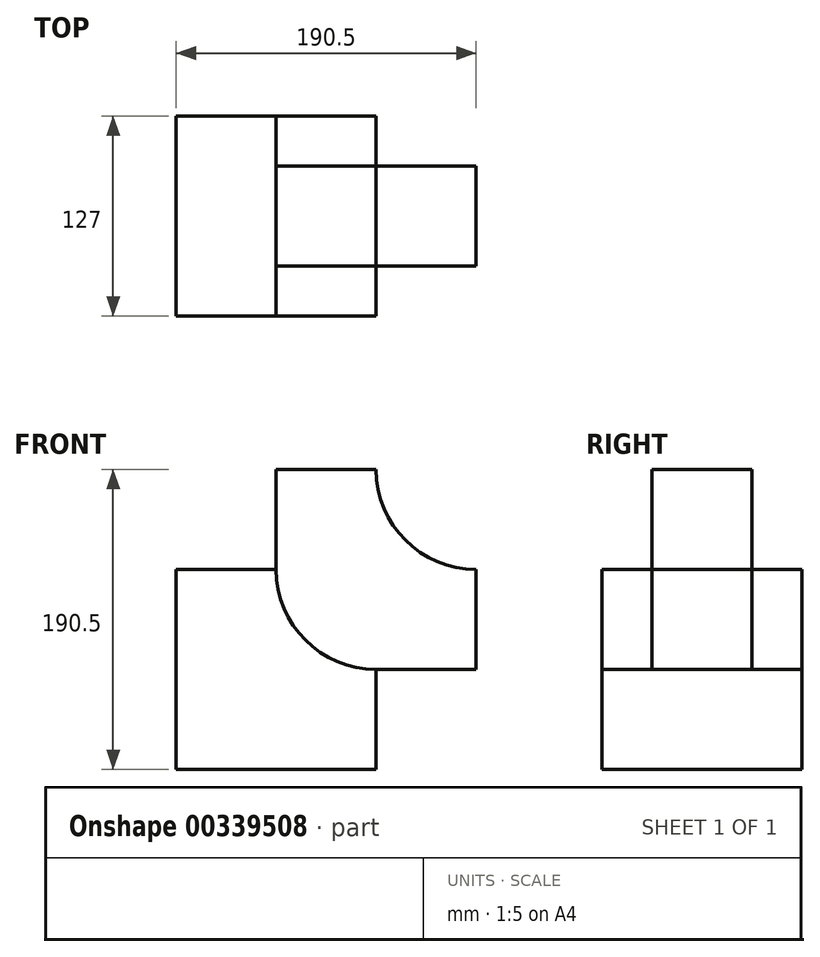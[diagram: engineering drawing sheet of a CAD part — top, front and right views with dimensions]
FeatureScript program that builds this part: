
annotation { "Feature Type Name" : "Feature", "Feature Type Description" : "" }
export const myFeature = defineFeature(function(context is Context, id is Id, definition is map)
    precondition{}
    {
        {
            var Q0;
            Q0=qCreatedBy(makeId("Front.planeOp"),FACE);
            var sketch = newSketch(context, id + "F0", { "sketchPlane" : qUnion([Q0])});
            skLineSegment(sketch, "E0.bottom", {"start": v(0, 63.5) * mm, "end": v(-63.5, 63.5) * mm});
            skLineSegment(sketch, "E0.top", {"start": v(63.5, -63.5) * mm, "end": v(-63.5, -63.5) * mm});
            skLineSegment(sketch, "E0.left", {"start": v(63.5, 0) * mm, "end": v(63.5, -63.5) * mm});
            skLineSegment(sketch, "E0.right", {"start": v(-63.5, 63.5) * mm, "end": v(-63.5, -63.5) * mm});
            skPoint(sketch, "E0.middle", {"position": v(0, 0) * mm});
            skArc(sketch, "E1", {"start": v(0, 63.5) * mm, "mid": v(18.6, 18.6) * mm, "end": v(63.5, 0) * mm});
            skSolve(sketch);
        }
        {
            var Q0;
            Q0=makeQuery(id+"F0.imprint","IMPRINT",FACE,{"disambiguationData":[TD([[makeQuery(id+"F0.imprint","IMPRINT",EDGE,{"derivedFrom":sQuery(id+"F0.wireOp",EDGE,"E0.bottom")}),1.0]])]});
            extrude(context, id + "F1", {"entities" : qUnion([Q0]), "endBound" : BoundingType.SYMMETRIC, "depth" : 127 * mm});
        }
        {
            var Q0;
            Q0=qCreatedBy(makeId("Front.planeOp"),FACE);
            var sketch = newSketch(context, id + "F2", { "sketchPlane" : qUnion([Q0])});
            skLineSegment(sketch, "E2.bottom", {"start": v(0, 0) * mm, "end": v(127, 0) * mm});
            skLineSegment(sketch, "E2.top", {"start": v(0, 127) * mm, "end": v(127, 127) * mm});
            skLineSegment(sketch, "E2.left", {"start": v(0, 0) * mm, "end": v(0, 127) * mm});
            skLineSegment(sketch, "E2.right", {"start": v(127, 0) * mm, "end": v(127, 127) * mm});
            skCircle(sketch, "E3", {"center": v(127, 127) * mm, "radius": 63.5 * mm});
            skSolve(sketch);
        }
        {
            var Q0;
            Q0=makeQuery(id+"F2.imprint","IMPRINT",FACE,{"disambiguationData":[TD([[makeQuery(id+"F2.imprint","IMPRINT",EDGE,{"derivedFrom":sQuery(id+"F2.wireOp",EDGE,"E2.bottom")}),1.0]])]});
            extrude(context, id + "F3", {"entities" : qUnion([Q0]), "operationType" : NewBodyOperationType.ADD, "endBound" : BoundingType.SYMMETRIC, "depth" : 63.5 * mm});
        }
    });
